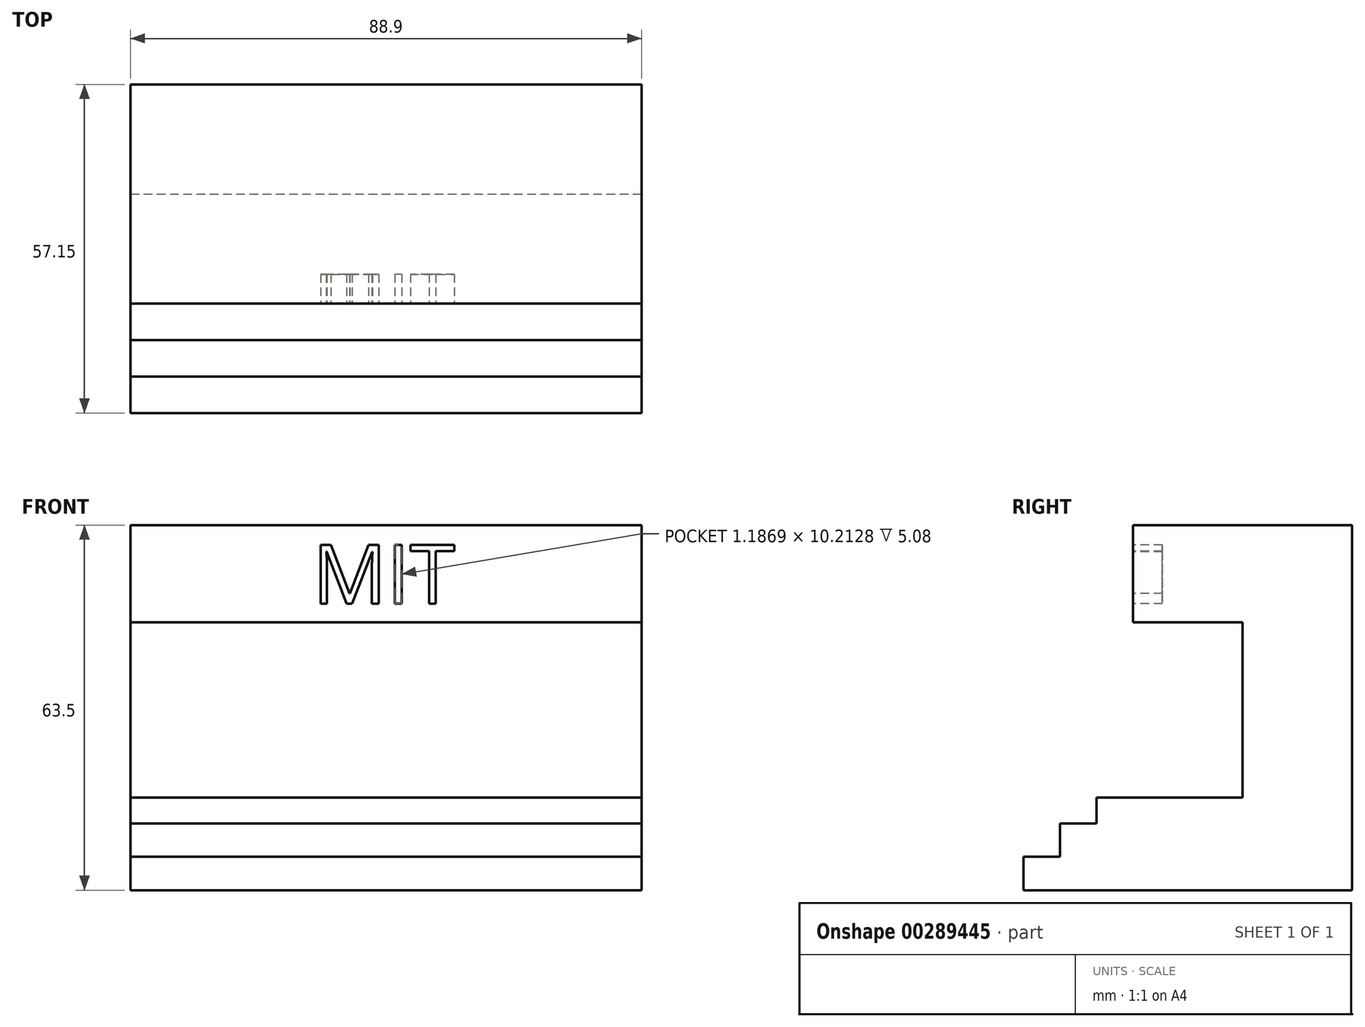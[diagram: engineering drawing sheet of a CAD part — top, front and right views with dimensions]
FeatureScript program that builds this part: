
annotation { "Feature Type Name" : "Feature", "Feature Type Description" : "" }
export const myFeature = defineFeature(function(context is Context, id is Id, definition is map)
    precondition{}
    {
        {
            var Q0;
            Q0=qCreatedBy(makeId("Top.planeOp"),FACE);
            var sketch = newSketch(context, id + "F0", { "sketchPlane" : qUnion([Q0])});
            skLineSegment(sketch, "E0.bottom", {"start": v(-45.56, 18.4) * mm, "end": v(43.34, 18.4) * mm});
            skLineSegment(sketch, "E0.top", {"start": v(-45.56, -19.7) * mm, "end": v(43.34, -19.7) * mm});
            skLineSegment(sketch, "E0.left", {"start": v(-45.56, 18.4) * mm, "end": v(-45.56, -19.7) * mm});
            skLineSegment(sketch, "E0.right", {"start": v(43.34, 18.4) * mm, "end": v(43.34, -19.7) * mm});
            skSolve(sketch);
        }
        {
            var Q0;
            Q0=makeQuery(id+"F0.imprint","IMPRINT",FACE,{"disambiguationData":[TD([[makeQuery(id+"F0.imprint","IMPRINT",EDGE,{"derivedFrom":sQuery(id+"F0.wireOp",EDGE,"E0.bottom")}),-1.0]])]});
            extrude(context, id + "F1", {"entities" : qUnion([Q0]), "depth" : 63.5 * mm});
        }
        {
            var Q0;
            Q0=makeQuery(id+"F1.opExtrude","SWEPT_FACE",FACE,{"disambiguationData":[OSD([sQuery(id+"F0.wireOp",EDGE,"E0.top")])]});
            var sketch = newSketch(context, id + "F2", { "sketchPlane" : qUnion([Q0])});
            skLineSegment(sketch, "E1.bottom", {"start": v(-45.56, 46.58) * mm, "end": v(43.34, 46.58) * mm});
            skLineSegment(sketch, "E1.top", {"start": v(-45.56, 16.1) * mm, "end": v(43.34, 16.1) * mm});
            skLineSegment(sketch, "E1.left", {"start": v(-45.56, 46.58) * mm, "end": v(-45.56, 16.1) * mm});
            skLineSegment(sketch, "E1.right", {"start": v(43.34, 46.58) * mm, "end": v(43.34, 16.1) * mm});
            skSolve(sketch);
        }
        {
            var Q0;
            Q0=makeQuery(id+"F2.imprint","IMPRINT",FACE,{"disambiguationData":[TD([[makeQuery(id+"F2.imprint","IMPRINT",EDGE,{"derivedFrom":sQuery(id+"F2.wireOp",EDGE,"E1.bottom")}),-1.0]])]});
            extrude(context, id + "F3", {"entities" : qUnion([Q0]), "operationType" : NewBodyOperationType.REMOVE, "oppositeDirection" : true, "depth" : 19.05 * mm});
        }
        {
            var Q0;
            {var subQ2=sQuery(id+"F0.wireOp",EDGE,"E0.top");Q0=makeQuery(id+"F3.boolean.opBoolean","SPLIT",FACE,{"disambiguationData":[TD([makeQuery(id+"F3.opExtrude","SWEPT_FACE",FACE,{"disambiguationData":[OSD([sQuery(id+"F2.wireOp",EDGE,"E1.top")])]})])],"derivedFrom":makeQuery(id+"F1.opExtrude","SWEPT_FACE",FACE,{"disambiguationData":[OSD([subQ2])]})});}
            var sketch = newSketch(context, id + "F4", { "sketchPlane" : qUnion([Q0])});
            skLineSegment(sketch, "E2.bottom", {"start": v(-45.56, 16.1) * mm, "end": v(43.34, 16.1) * mm});
            skLineSegment(sketch, "E2.top", {"start": v(-45.56, 11.57) * mm, "end": v(43.34, 11.57) * mm});
            skLineSegment(sketch, "E2.left", {"start": v(-45.56, 16.1) * mm, "end": v(-45.56, 11.57) * mm});
            skLineSegment(sketch, "E2.right", {"start": v(43.34, 16.1) * mm, "end": v(43.34, 11.57) * mm});
            skSolve(sketch);
        }
        {
            var Q0;
            Q0=makeQuery(id+"F4.imprint","IMPRINT",FACE,{"disambiguationData":[TD([[makeQuery(id+"F4.imprint","IMPRINT",EDGE,{"derivedFrom":sQuery(id+"F4.wireOp",EDGE,"E2.bottom")}),-1.0]])]});
            extrude(context, id + "F5", {"entities" : qUnion([Q0]), "operationType" : NewBodyOperationType.ADD, "depth" : 6.35 * mm});
        }
        {
            var Q0;
            {var subQ2=sQuery(id+"F0.wireOp",EDGE,"E0.top");Q0=makeQuery(id+"F3.boolean.opBoolean","SPLIT",FACE,{"disambiguationData":[TD([makeQuery(id+"F3.opExtrude","SWEPT_FACE",FACE,{"disambiguationData":[OSD([sQuery(id+"F2.wireOp",EDGE,"E1.top")])]})])],"derivedFrom":makeQuery(id+"F1.opExtrude","SWEPT_FACE",FACE,{"disambiguationData":[OSD([subQ2])]})});}
            var sketch = newSketch(context, id + "F6", { "sketchPlane" : qUnion([Q0])});
            skLineSegment(sketch, "E3.bottom", {"start": v(-45.56, 11.57) * mm, "end": v(43.34, 11.57) * mm});
            skLineSegment(sketch, "E3.top", {"start": v(-45.56, 5.79) * mm, "end": v(43.34, 5.79) * mm});
            skLineSegment(sketch, "E3.left", {"start": v(-45.56, 11.57) * mm, "end": v(-45.56, 5.79) * mm});
            skLineSegment(sketch, "E3.right", {"start": v(43.34, 11.57) * mm, "end": v(43.34, 5.79) * mm});
            skSolve(sketch);
        }
        {
            var Q0;
            Q0=makeQuery(id+"F6.imprint","IMPRINT",FACE,{"disambiguationData":[TD([[makeQuery(id+"F6.imprint","IMPRINT",EDGE,{"derivedFrom":sQuery(id+"F6.wireOp",EDGE,"E3.bottom")}),-1.0]])]});
            extrude(context, id + "F7", {"entities" : qUnion([Q0]), "operationType" : NewBodyOperationType.ADD, "depth" : 12.7 * mm});
        }
        {
            var Q0;
            {var subQ2=sQuery(id+"F0.wireOp",EDGE,"E0.top");Q0=makeQuery(id+"F3.boolean.opBoolean","SPLIT",FACE,{"disambiguationData":[TD([makeQuery(id+"F3.opExtrude","SWEPT_FACE",FACE,{"disambiguationData":[OSD([sQuery(id+"F2.wireOp",EDGE,"E1.top")])]})])],"derivedFrom":makeQuery(id+"F1.opExtrude","SWEPT_FACE",FACE,{"disambiguationData":[OSD([subQ2])]})});}
            var sketch = newSketch(context, id + "F8", { "sketchPlane" : qUnion([Q0])});
            skLineSegment(sketch, "E4.bottom", {"start": v(-45.56, 5.79) * mm, "end": v(43.34, 5.79) * mm});
            skLineSegment(sketch, "E4.top", {"start": v(-45.56, 0) * mm, "end": v(43.34, 0) * mm});
            skLineSegment(sketch, "E4.left", {"start": v(-45.56, 5.79) * mm, "end": v(-45.56, 0) * mm});
            skLineSegment(sketch, "E4.right", {"start": v(43.34, 5.79) * mm, "end": v(43.34, 0) * mm});
            skSolve(sketch);
        }
        {
            var Q0;
            Q0=makeQuery(id+"F8.imprint","IMPRINT",FACE,{"disambiguationData":[TD([[makeQuery(id+"F8.imprint","IMPRINT",EDGE,{"derivedFrom":sQuery(id+"F8.wireOp",EDGE,"E4.bottom")}),-1.0]])]});
            extrude(context, id + "F9", {"entities" : qUnion([Q0]), "operationType" : NewBodyOperationType.ADD, "depth" : 19.05 * mm});
        }
        {
            var Q0;
            {var subQ2=sQuery(id+"F0.wireOp",EDGE,"E0.top");Q0=makeQuery(id+"F3.boolean.opBoolean","SPLIT",FACE,{"disambiguationData":[TD([makeQuery(id+"F3.opExtrude","SWEPT_FACE",FACE,{"disambiguationData":[OSD([sQuery(id+"F2.wireOp",EDGE,"E1.bottom")])]})])],"derivedFrom":makeQuery(id+"F1.opExtrude","SWEPT_FACE",FACE,{"disambiguationData":[OSD([subQ2])]})});}
            var sketch = newSketch(context, id + "F10", { "sketchPlane" : qUnion([Q0])});
            skText(sketch, "E5", { "text": "MIT", "fontName": "OpenSans-Regular.ttf"});
            const initialGuessF10  = {"E5": [-0.0139, 0.04983, 1, 0, 0.0103]};
            skSetInitialGuess(sketch, initialGuessF10);
            skSolve(sketch);
        }
        {
            var Q0;
            Q0 = qSketchRegion(id + "F10", true);
            extrude(context, id + "F11", {"entities" : qUnion([Q0]), "operationType" : NewBodyOperationType.REMOVE, "oppositeDirection" : true, "depth" : 5.08 * mm});
        }
    });
